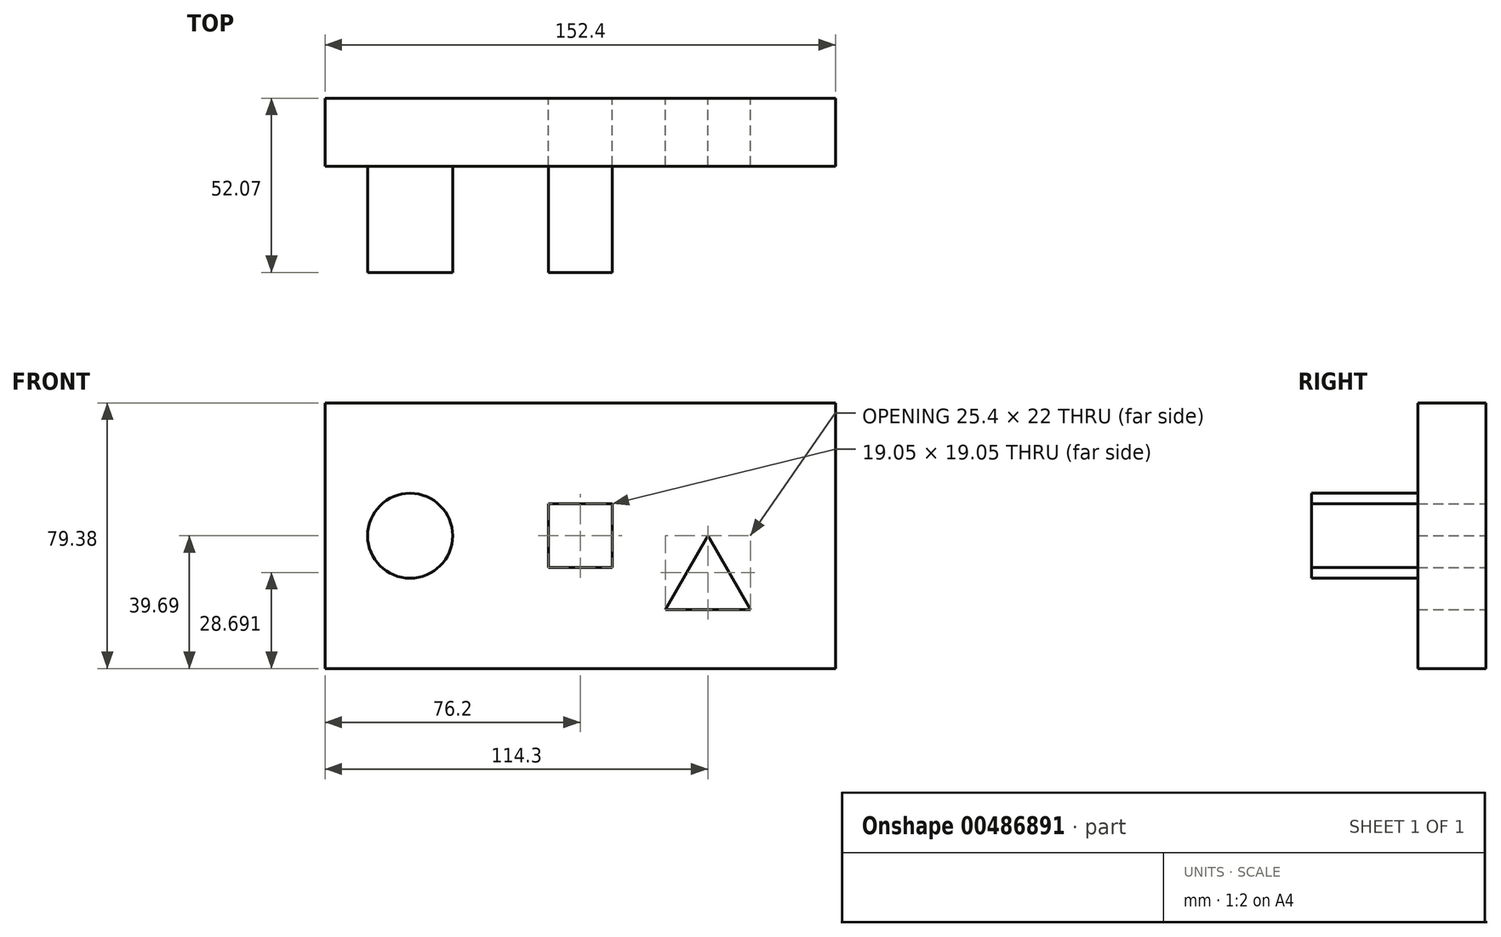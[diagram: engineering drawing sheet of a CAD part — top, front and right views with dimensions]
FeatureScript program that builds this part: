
annotation { "Feature Type Name" : "Feature", "Feature Type Description" : "" }
export const myFeature = defineFeature(function(context is Context, id is Id, definition is map)
    precondition{}
    {
        {
            var Q0;
            Q0=qCreatedBy(makeId("Front.planeOp"),FACE);
            var sketch = newSketch(context, id + "F0", { "sketchPlane" : qUnion([Q0])});
            skPoint(sketch, "E0", {"position": v(44.45, 0) * mm});
            skPoint(sketch, "E1", {"position": v(-31.75, 0) * mm});
            skPoint(sketch, "E2", {"position": v(-82.55, 0) * mm});
            skCircle(sketch, "E3", {"center": v(-82.55, 0) * mm, "radius": 12.7 * mm});
            skLineSegment(sketch, "E4.bottom", {"start": v(-22.22, 9.52) * mm, "end": v(-41.27, 9.53) * mm});
            skLineSegment(sketch, "E4.top", {"start": v(-22.23, -9.53) * mm, "end": v(-41.27, -9.52) * mm});
            skLineSegment(sketch, "E4.left", {"start": v(-22.22, 9.52) * mm, "end": v(-22.23, -9.53) * mm});
            skLineSegment(sketch, "E4.right", {"start": v(-41.27, 9.53) * mm, "end": v(-41.27, -9.52) * mm});
            skPoint(sketch, "E5", {"position": v(6.35, 0) * mm});
            skLineSegment(sketch, "E6", {"start": v(6.35, 0) * mm, "end": v(-6.35, -22) * mm});
            skLineSegment(sketch, "E7", {"start": v(-6.35, -22) * mm, "end": v(19.05, -22) * mm});
            skLineSegment(sketch, "E8", {"start": v(19.05, -22) * mm, "end": v(6.35, 0) * mm});
            skLineSegment(sketch, "E9", {"start": v(44.45, 0) * mm, "end": v(44.45, -39.69) * mm});
            skLineSegment(sketch, "E10", {"start": v(44.45, 0) * mm, "end": v(44.45, 39.69) * mm});
            skLineSegment(sketch, "E11", {"start": v(44.45, 39.69) * mm, "end": v(-107.95, 39.69) * mm});
            skLineSegment(sketch, "E12", {"start": v(-107.95, 39.69) * mm, "end": v(-107.95, -39.69) * mm});
            skLineSegment(sketch, "E13", {"start": v(-107.95, -39.69) * mm, "end": v(44.45, -39.69) * mm});
            skSolve(sketch);
        }
        {
            var Q0;
            Q0=makeQuery(id+"F0.imprint","IMPRINT",FACE,{"disambiguationData":[TD([[makeQuery(id+"F0.imprint","IMPRINT",EDGE,{"derivedFrom":sQuery(id+"F0.wireOp",EDGE,"E3")}),-1.0]])]});
            extrude(context, id + "F1", {"entities" : qUnion([Q0]), "depth" : 20.32 * mm});
        }
        {
            var Q0;
            Q0=makeQuery(id+"F0.imprint","IMPRINT",FACE,{"disambiguationData":[TD([[makeQuery(id+"F0.imprint","IMPRINT",EDGE,{"derivedFrom":sQuery(id+"F0.wireOp",EDGE,"E3")}),1.0]])]});
            extrude(context, id + "F2", {"entities" : qUnion([Q0]), "operationType" : NewBodyOperationType.ADD, "depth" : 52.07 * mm});
        }
        {
            var Q0;
            Q0=makeQuery(id+"F0.imprint","IMPRINT",FACE,{"disambiguationData":[TD([[makeQuery(id+"F0.imprint","IMPRINT",EDGE,{"derivedFrom":sQuery(id+"F0.wireOp",EDGE,"E4.bottom")}),1.0]])]});
            extrude(context, id + "F3", {"entities" : qUnion([Q0]), "operationType" : NewBodyOperationType.ADD, "depth" : 52.07 * mm});
        }
        {
            var Q0;
            Q0=makeQuery(id+"F0.imprint","IMPRINT",FACE,{"disambiguationData":[TD([[makeQuery(id+"F0.imprint","IMPRINT",EDGE,{"derivedFrom":sQuery(id+"F0.wireOp",EDGE,"E4.bottom")}),1.0]])]});
            extrude(context, id + "F4", {"entities" : qUnion([Q0]), "operationType" : NewBodyOperationType.REMOVE, "depth" : 20.32 * mm});
        }
    });
